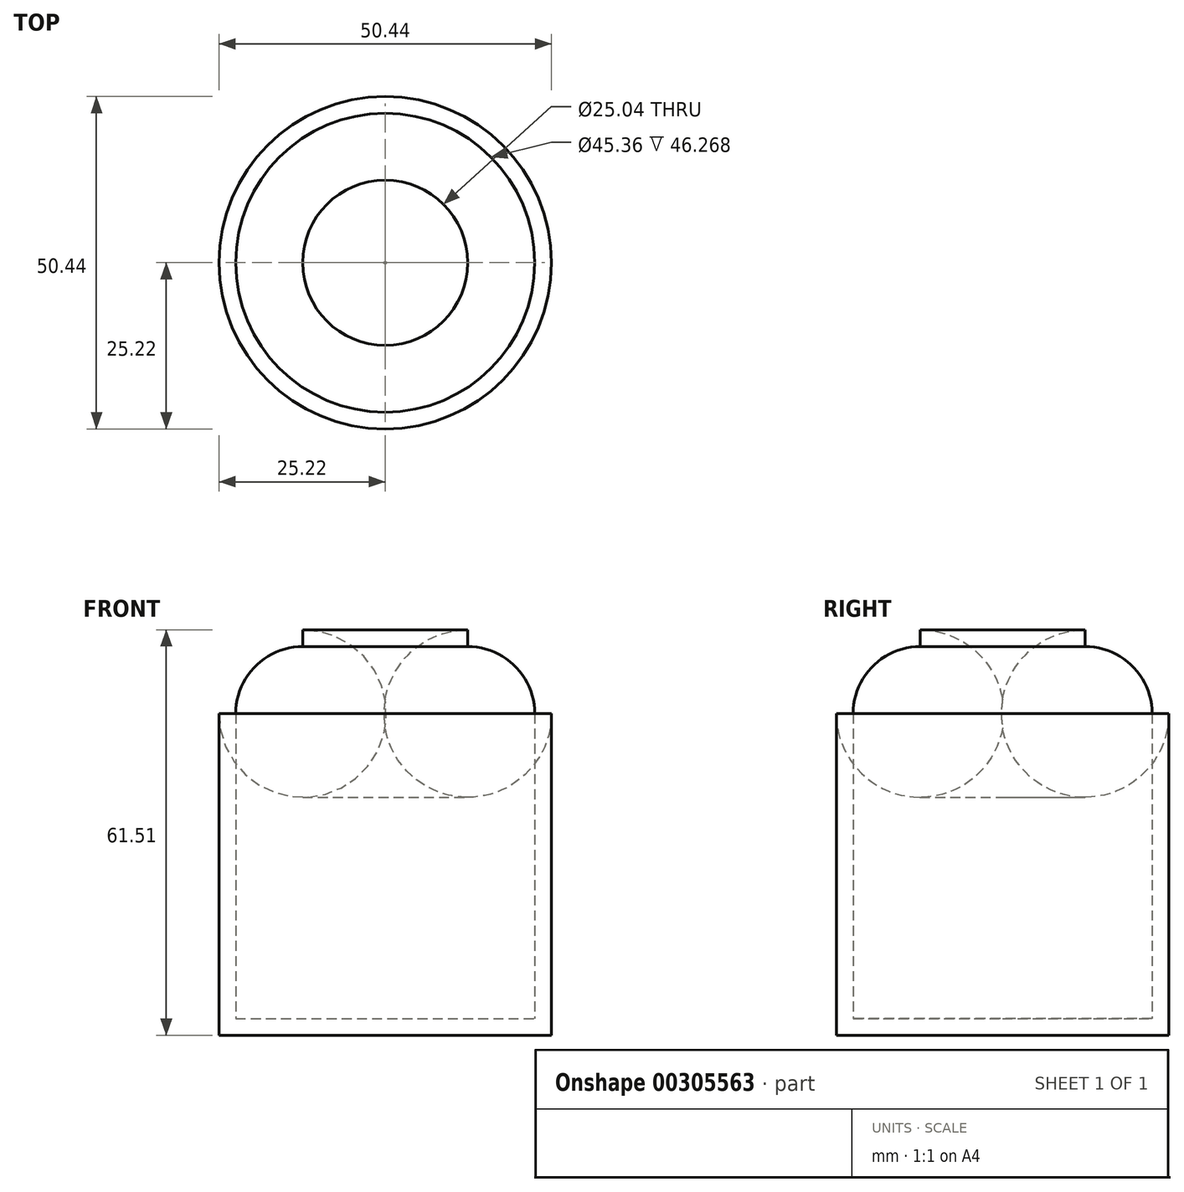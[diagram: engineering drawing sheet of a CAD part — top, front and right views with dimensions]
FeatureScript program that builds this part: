
annotation { "Feature Type Name" : "Feature", "Feature Type Description" : "" }
export const myFeature = defineFeature(function(context is Context, id is Id, definition is map)
    precondition{}
    {
        {
            var Q0;
            Q0=qCreatedBy(makeId("Front.planeOp"),FACE);
            var sketch = newSketch(context, id + "F0", { "sketchPlane" : qUnion([Q0])});
            skLineSegment(sketch, "E0.bottom", {"start": v(0, 0) * mm, "end": v(25.22, 0) * mm});
            skLineSegment(sketch, "E0.top", {"start": v(0, 61.5) * mm, "end": v(25.22, 61.5) * mm});
            skLineSegment(sketch, "E0.left", {"start": v(0, 0) * mm, "end": v(0, 61.5) * mm});
            skLineSegment(sketch, "E0.right", {"start": v(25.22, 0) * mm, "end": v(25.22, 61.5) * mm});
            skSolve(sketch);
        }
        {
            var Q0;
            Q0=makeQuery(id+"F0.imprint","IMPRINT",FACE,{"disambiguationData":[TD([[makeQuery(id+"F0.imprint","IMPRINT",EDGE,{"derivedFrom":sQuery(id+"F0.wireOp",EDGE,"E0.bottom")}),1.0]])]});
            var Q1;
            Q1=sQuery(id+"F0.wireOp",EDGE,"E0.left");
            revolve(context, id + "F1", {"entities" : qUnion([Q0]), "axis" : qUnion([Q1]), "revolveType" : RevolveType.FULL});
        }
        {
            var Q0;
            Q0=makeQuery(id+"F1.opRevolve","SWEPT_FACE",FACE,{"disambiguationData":[OSD([sQuery(id+"F0.wireOp",EDGE,"E0.top")])]});
            fillet(context, id + "F2", {"entities" : qUnion([Q0]), "radius" : 12.7 * mm, "tangentPropagation" : true, "allowEdgeOverflow" : false});
        }
        {
            var Q0;
            Q0=makeQuery(id+"F1.opRevolve","SWEPT_FACE",FACE,{"disambiguationData":[OSD([sQuery(id+"F0.wireOp",EDGE,"E0.top")])]});
            shell(context, id + "F3", {"entities" : qUnion([Q0]), "thickness" : 2.54 * mm});
        }
    });
